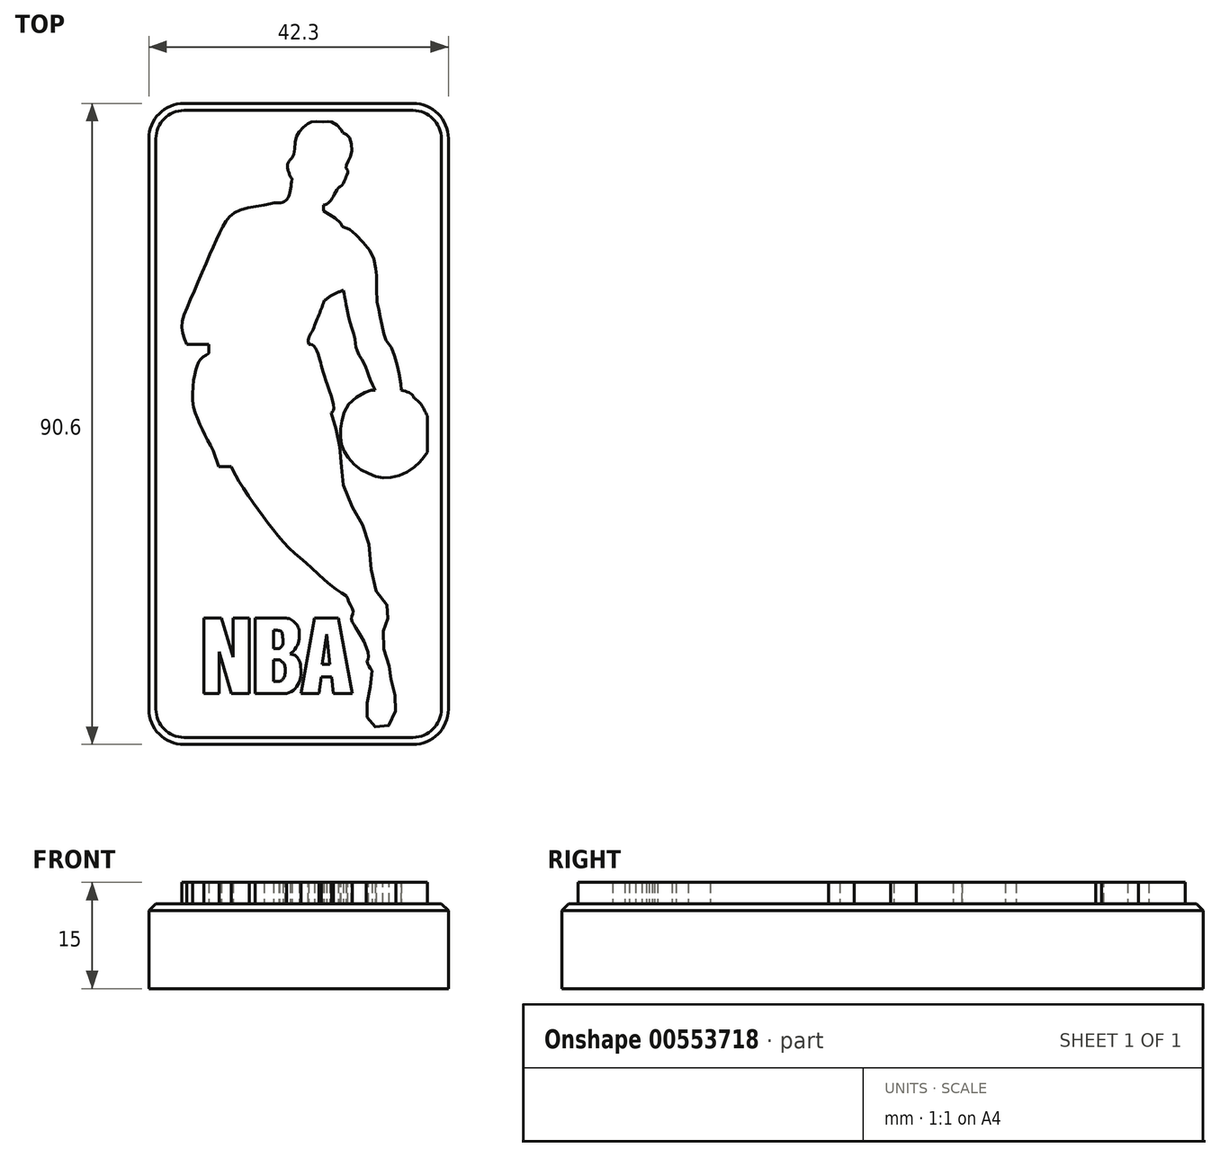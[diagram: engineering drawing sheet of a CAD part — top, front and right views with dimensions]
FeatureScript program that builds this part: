
annotation { "Feature Type Name" : "Feature", "Feature Type Description" : "" }
export const myFeature = defineFeature(function(context is Context, id is Id, definition is map)
    precondition{}
    {
        {
            var Q0;
            Q0=qCreatedBy(makeId("Top.planeOp"),FACE);
            var sketch = newSketch(context, id + "F0", { "sketchPlane" : qUnion([Q0])});
            skLineSegment(sketch, "E0", {"start": v(49.46, 96.34) * mm, "end": v(49.46, 0) * mm, "construction": true});
            skLineSegment(sketch, "E1", {"start": v(0, 48.17) * mm, "end": v(98.91, 48.17) * mm, "construction": true});
            skLineSegment(sketch, "E2.bottom", {"start": v(70.6, 93.47) * mm, "end": v(28.3, 93.47) * mm});
            skLineSegment(sketch, "E2.top", {"start": v(70.6, 2.87) * mm, "end": v(28.3, 2.87) * mm});
            skLineSegment(sketch, "E2.left", {"start": v(70.6, 93.47) * mm, "end": v(70.6, 2.87) * mm});
            skLineSegment(sketch, "E2.right", {"start": v(28.3, 93.47) * mm, "end": v(28.3, 2.87) * mm});
            skPoint(sketch, "E2.middle", {"position": v(49.46, 48.17) * mm});
            skSolve(sketch);
        }
        {
            var Q0;
            Q0=qSketchRegion(id+"F0",true);
            extrude(context, id + "F1", {"entities" : qUnion([Q0]), "depth" : 12 * mm, "offsetDistance" : 25 * mm});
        }
        {
            var Q0;
            Q0=qCreatedBy(makeId("Top.planeOp"),FACE);
            var sketch = newSketch(context, id + "F2", { "sketchPlane" : qUnion([Q0])});
            skLineSegment(sketch, "E3", {"start": v(36.08, 10.07) * mm, "end": v(36.06, 20.74) * mm});
            skLineSegment(sketch, "E4", {"start": v(36.06, 20.74) * mm, "end": v(38.53, 20.74) * mm});
            skLineSegment(sketch, "E5", {"start": v(38.53, 20.74) * mm, "end": v(40.2, 15.23) * mm});
            skLineSegment(sketch, "E6", {"start": v(40.2, 15.23) * mm, "end": v(40.2, 20.74) * mm});
            skLineSegment(sketch, "E7", {"start": v(40.2, 20.74) * mm, "end": v(42.53, 20.74) * mm});
            skLineSegment(sketch, "E8", {"start": v(42.53, 20.74) * mm, "end": v(42.53, 10.07) * mm});
            skLineSegment(sketch, "E9", {"start": v(42.53, 10.07) * mm, "end": v(39.96, 10.07) * mm});
            skLineSegment(sketch, "E10", {"start": v(39.96, 10.07) * mm, "end": v(38.25, 15.94) * mm});
            skLineSegment(sketch, "E11", {"start": v(38.25, 15.94) * mm, "end": v(38.25, 10.07) * mm});
            skLineSegment(sketch, "E12", {"start": v(38.25, 10.07) * mm, "end": v(36.08, 10.07) * mm});
            skLineSegment(sketch, "E13", {"start": v(43.32, 10.07) * mm, "end": v(43.3, 20.74) * mm});
            skLineSegment(sketch, "E14", {"start": v(43.3, 20.74) * mm, "end": v(47.68, 20.74) * mm});
            skLineSegment(sketch, "E15", {"start": v(43.32, 10.07) * mm, "end": v(47.75, 10.08) * mm});
            skFitSpline(sketch, "E16", {"points": [v(47.75, 10.08) * mm, v(48.77, 10.58) * mm, v(49.49, 11.58) * mm, v(49.77, 12.75) * mm, v(49.75, 13.92) * mm, v(49.51, 14.83) * mm, v(49.15, 15.29) * mm, v(48.83, 15.52) * mm, v(48.28, 15.65) * mm], "startDerivative": vector(7.59, 2.72) * mm, "endDerivative": vector(-5.94, 1) * mm});
            skFitSpline(sketch, "E17", {"points": [v(48.28, 15.65) * mm, v(48.94, 16.33) * mm, v(49.47, 17.44) * mm, v(49.53, 18.32) * mm, v(49.49, 19.2) * mm, v(49.21, 19.77) * mm, v(48.72, 20.3) * mm, v(48.28, 20.6) * mm, v(47.68, 20.74) * mm], "startDerivative": vector(4.95, 4.43) * mm, "endDerivative": vector(-5.76, 0.93) * mm});
            skLineSegment(sketch, "E18", {"start": v(45.94, 19) * mm, "end": v(45.94, 16.5) * mm});
            skFitSpline(sketch, "E19", {"points": [v(45.94, 19) * mm, v(46.53, 19) * mm, v(47, 18.82) * mm, v(47.2, 18.33) * mm, v(47.25, 17.67) * mm, v(47.25, 17.06) * mm, v(46.99, 16.64) * mm, v(46.7, 16.44) * mm], "startDerivative": vector(3.88, 0.21) * mm, "endDerivative": vector(-2.46, -1.47) * mm});
            skLineSegment(sketch, "E20", {"start": v(46.7, 16.44) * mm, "end": v(45.94, 16.44) * mm});
            skLineSegment(sketch, "E21", {"start": v(45.94, 16.44) * mm, "end": v(45.94, 16.5) * mm});
            skLineSegment(sketch, "E22", {"start": v(45.94, 14.83) * mm, "end": v(45.94, 11.81) * mm});
            skLineSegment(sketch, "E23", {"start": v(45.94, 11.81) * mm, "end": v(46.79, 11.81) * mm});
            skFitSpline(sketch, "E24", {"points": [v(46.79, 11.81) * mm, v(47.22, 12.07) * mm, v(47.53, 12.8) * mm, v(47.56, 13.65) * mm, v(47.4, 14.25) * mm, v(47, 14.66) * mm, v(46.79, 14.84) * mm], "startDerivative": vector(3, 1.25) * mm, "endDerivative": vector(-1.62, 1.47) * mm});
            skLineSegment(sketch, "E25", {"start": v(45.94, 14.83) * mm, "end": v(46.79, 14.84) * mm});
            skLineSegment(sketch, "E26", {"start": v(49.8, 10.08) * mm, "end": v(50.27, 10.08) * mm});
            skLineSegment(sketch, "E27", {"start": v(50.27, 10.08) * mm, "end": v(52.35, 10.09) * mm});
            skLineSegment(sketch, "E28", {"start": v(52.35, 10.09) * mm, "end": v(52.64, 12.4) * mm});
            skLineSegment(sketch, "E29", {"start": v(52.64, 12.4) * mm, "end": v(54.13, 12.4) * mm});
            skLineSegment(sketch, "E30", {"start": v(54.13, 12.4) * mm, "end": v(54.35, 10.08) * mm});
            skLineSegment(sketch, "E31", {"start": v(54.35, 10.08) * mm, "end": v(57.02, 10.1) * mm});
            skLineSegment(sketch, "E32", {"start": v(57.02, 10.1) * mm, "end": v(55.07, 20.7) * mm});
            skLineSegment(sketch, "E33", {"start": v(55.07, 20.7) * mm, "end": v(51.71, 20.7) * mm});
            skLineSegment(sketch, "E34", {"start": v(51.71, 20.7) * mm, "end": v(49.8, 10.08) * mm});
            skLineSegment(sketch, "E35", {"start": v(52.8, 14.19) * mm, "end": v(53.85, 14.19) * mm});
            skLineSegment(sketch, "E36", {"start": v(53.85, 14.19) * mm, "end": v(53.45, 18.42) * mm});
            skLineSegment(sketch, "E37", {"start": v(53.45, 18.42) * mm, "end": v(52.8, 14.19) * mm});
            skSolve(sketch);
        }
        {
            var Q0;
            Q0=qSketchRegion(id+"F2",true);
            extrude(context, id + "F3", {"entities" : qUnion([Q0]), "operationType" : NewBodyOperationType.ADD, "depth" : 15 * mm, "offsetDistance" : 25 * mm});
        }
        {
            var Q0;
            Q0=qCreatedBy(makeId("Top.planeOp"),FACE);
            var sketch = newSketch(context, id + "F4", { "sketchPlane" : qUnion([Q0])});
            skFitSpline(sketch, "E38", {"points": [v(56.13, 84.27) * mm, v(56.38, 84.06) * mm, v(56.32, 83.43) * mm, v(56.07, 82.86) * mm, v(55.63, 81.93) * mm, v(55.23, 81.64) * mm, v(55.06, 81.53) * mm, v(54.6, 80.79) * mm, v(54.22, 80.1) * mm, v(53.88, 79.58) * mm, v(53.44, 79.24) * mm, v(52.94, 79.1) * mm], "startDerivative": vector(4.5, -2.2) * mm, "endDerivative": vector(-5.95, -1.06) * mm});
            skFitSpline(sketch, "E39", {"points": [v(52.94, 79.1) * mm, v(52.94, 78.25) * mm], "startDerivative": vector(0, -0.86) * mm, "endDerivative": vector(0, -0.86) * mm});
            skFitSpline(sketch, "E40", {"points": [v(52.94, 78.25) * mm, v(55.23, 76.82) * mm, v(55.42, 76.5) * mm, v(55.44, 76.18) * mm, v(56.1, 75.95) * mm, v(57.05, 75.4) * mm, v(58.11, 74.32) * mm, v(59.44, 72.75) * mm, v(60.08, 71.4) * mm, v(60.4, 69.88) * mm, v(60.48, 68.98) * mm, v(60.5, 65.62) * mm, v(60.72, 64.46) * mm, v(60.95, 63.55) * mm, v(61.19, 62.38) * mm, v(61.46, 61.03) * mm, v(61.64, 60.25) * mm, v(62.44, 59.13) * mm, v(63.02, 57.81) * mm, v(63.42, 56.2) * mm, v(63.72, 55.04) * mm, v(63.95, 53.3) * mm, v(63.93, 52.94) * mm], "startDerivative": vector(43.04, -24.8) * mm, "endDerivative": vector(-1.36, -11.13) * mm});
            skFitSpline(sketch, "E41", {"points": [v(63.93, 52.94) * mm, v(65.3, 52.44) * mm, v(65.82, 51.82) * mm, v(66.57, 51.15) * mm, v(67.18, 50.18) * mm, v(67.65, 49.33) * mm], "startDerivative": vector(6.8, -1.68) * mm, "endDerivative": vector(2.4, -4.31) * mm});
            skFitSpline(sketch, "E42", {"points": [v(67.65, 49.33) * mm, v(67.65, 44.18) * mm], "startDerivative": vector(0, -5.16) * mm, "endDerivative": vector(0, -5.16) * mm});
            skFitSpline(sketch, "E43", {"points": [v(67.65, 44.18) * mm, v(66.97, 43.24) * mm, v(66.13, 42.32) * mm, v(64.47, 41.17) * mm, v(62.47, 40.6) * mm, v(60.8, 40.62) * mm, v(59.17, 41.23) * mm, v(57.4, 42.34) * mm, v(56.09, 43.95) * mm, v(55.52, 45.24) * mm, v(55.39, 47.05) * mm, v(55.66, 48.91) * mm, v(56.6, 51.04) * mm, v(58.92, 52.66) * mm, v(59.94, 52.94) * mm, v(60.26, 52.94) * mm], "startDerivative": vector(-11.97, -17.16) * mm, "endDerivative": vector(9.83, -0.58) * mm});
            skFitSpline(sketch, "E44", {"points": [v(60.26, 52.94) * mm, v(59.23, 55.35) * mm, v(58.66, 56.77) * mm, v(57.7, 58.56) * mm, v(57.43, 59.99) * mm, v(56.7, 62.7) * mm, v(56.23, 64.65) * mm, v(55.98, 66) * mm, v(55.78, 67.05) * mm], "startDerivative": vector(-7.83, 17.22) * mm, "endDerivative": vector(-2.09, 10.68) * mm});
            skFitSpline(sketch, "E45", {"points": [v(55.78, 67.05) * mm, v(54.3, 66.44) * mm, v(53.03, 65.52) * mm], "startDerivative": vector(-3.05, -1.05) * mm, "endDerivative": vector(-2.45, -2) * mm});
            skFitSpline(sketch, "E46", {"points": [v(53.03, 65.52) * mm, v(52.58, 64.2) * mm, v(51.95, 62.72) * mm, v(51.36, 61.21) * mm, v(50.82, 60.12) * mm, v(50.91, 59.4) * mm], "startDerivative": vector(-1.92, -6.3) * mm, "endDerivative": vector(1.44, -4.65) * mm});
            skFitSpline(sketch, "E47", {"points": [v(50.91, 59.4) * mm, v(51.55, 59.24) * mm, v(52.44, 57.38) * mm, v(53.03, 55.16) * mm, v(54.43, 50.33) * mm, v(54.05, 49.77) * mm], "startDerivative": vector(5.44, 0.14) * mm, "endDerivative": vector(-4.4, -2.9) * mm});
            skFitSpline(sketch, "E48", {"points": [v(54.05, 49.77) * mm, v(54.73, 47.48) * mm, v(55.23, 45.12) * mm, v(55.52, 41.97) * mm, v(55.78, 39.46) * mm, v(57.5, 35.56) * mm, v(58.9, 33.04) * mm, v(59.62, 29) * mm, v(60.26, 24.8) * mm, v(61.78, 22.84) * mm, v(62.25, 21.32) * mm, v(61.75, 19.99) * mm, v(61.41, 18.58) * mm, v(61.55, 15.9) * mm, v(62.25, 13.82) * mm, v(62.39, 12.62) * mm, v(62.93, 10.42) * mm, v(63.18, 8.86) * mm, v(62.96, 6.61) * mm, v(61.78, 5.28) * mm, v(60.26, 5.35) * mm, v(59.38, 6.27) * mm, v(59.04, 7.27) * mm, v(59.24, 9.2) * mm, v(59.62, 11.3) * mm, v(59.8, 13.32) * mm], "startDerivative": vector(17.19, -55.33) * mm, "endDerivative": vector(3.4, 52.46) * mm});
            skFitSpline(sketch, "E49", {"points": [v(59.8, 13.32) * mm, v(59.38, 13.98) * mm, v(59.13, 14.61) * mm, v(59.35, 15.3) * mm, v(58.15, 18.35) * mm, v(57.15, 19.96) * mm, v(56.93, 20.92) * mm, v(57.18, 21.57) * mm, v(56.68, 22.77) * mm, v(56.25, 23.86) * mm], "startDerivative": vector(-4.75, 7.09) * mm, "endDerivative": vector(-3.14, 9.49) * mm});
            skFitSpline(sketch, "E50", {"points": [v(56.25, 23.86) * mm, v(54.05, 25.32) * mm, v(50.91, 28.18) * mm, v(48.25, 30.48) * mm, v(45.53, 33.66) * mm, v(43.03, 37.06) * mm, v(40.69, 40.68) * mm, v(39.95, 42.15) * mm], "startDerivative": vector(-17, 10) * mm, "endDerivative": vector(-6.02, 13.27) * mm});
            skFitSpline(sketch, "E51", {"points": [v(39.95, 42.15) * mm, v(38.15, 42.15) * mm], "startDerivative": vector(-1.8, 0) * mm, "endDerivative": vector(-1.8, 0) * mm});
            skFitSpline(sketch, "E52", {"points": [v(38.15, 42.15) * mm, v(37.48, 44.18) * mm, v(36.33, 46.41) * mm, v(35.3, 48.66) * mm, v(34.52, 51.21) * mm, v(34.68, 54.49) * mm, v(35.06, 56.2) * mm, v(35.44, 57.08) * mm, v(36.09, 57.7) * mm, v(36.8, 58.11) * mm], "startDerivative": vector(-4.74, 16.89) * mm, "endDerivative": vector(9.78, 5.16) * mm});
            skFitSpline(sketch, "E53", {"points": [v(36.8, 58.11) * mm, v(36.8, 59.4) * mm], "startDerivative": vector(0, 1.3) * mm, "endDerivative": vector(0, 1.3) * mm});
            skFitSpline(sketch, "E54", {"points": [v(36.8, 59.4) * mm, v(33.68, 59.4) * mm], "startDerivative": vector(-3.13, 0) * mm, "endDerivative": vector(-3.13, 0) * mm});
            skFitSpline(sketch, "E55", {"points": [v(33.68, 59.4) * mm, v(32.96, 61.88) * mm, v(34.1, 65.52) * mm, v(36.8, 71.87) * mm, v(38.68, 75.91) * mm, v(40.4, 78) * mm, v(44.62, 79.07) * mm], "startDerivative": vector(-8.1, 18.08) * mm, "endDerivative": vector(27.69, 3.84) * mm});
            skFitSpline(sketch, "E56", {"points": [v(44.62, 79.07) * mm, v(45.92, 79.38) * mm, v(46.95, 79.42) * mm, v(47.86, 79.95) * mm, v(48.24, 80.94) * mm, v(48.51, 82.77) * mm], "startDerivative": vector(6.45, 2) * mm, "endDerivative": vector(1.03, 8.03) * mm});
            skFitSpline(sketch, "E57", {"points": [v(48.51, 82.77) * mm, v(48.02, 83.84) * mm, v(47.94, 84.94) * mm, v(48.51, 85.74) * mm], "startDerivative": vector(-1.61, 2.97) * mm, "endDerivative": vector(2.25, 2.32) * mm});
            skFitSpline(sketch, "E58", {"points": [v(48.51, 85.74) * mm, v(48.85, 86.5) * mm, v(49.05, 88.41) * mm, v(49.7, 89.67) * mm, v(50.91, 90.7) * mm, v(51.52, 90.9) * mm, v(53.31, 90.85) * mm, v(54.05, 90.9) * mm, v(55.33, 89.86) * mm, v(55.78, 89.25) * mm, v(56.36, 88.98) * mm, v(56.97, 87.38) * mm, v(56.7, 85.74) * mm, v(56.23, 84.8) * mm, v(56.13, 84.27) * mm], "startDerivative": vector(6.68, 10.5) * mm, "endDerivative": vector(-0.94, -10.26) * mm});
            skSolve(sketch);
        }
        {
            var Q0;
            Q0=qSketchRegion(id+"F4",true);
            extrude(context, id + "F5", {"entities" : qUnion([Q0]), "operationType" : NewBodyOperationType.ADD, "depth" : 15 * mm, "offsetDistance" : 25 * mm});
        }
        {
            var Q0;
            Q0=makeQuery(id+"F1.opExtrude","SWEPT_EDGE",EDGE,{"disambiguationData":[OSD([sQuery(id+"F0.wireOp",EDGE,"E2.bottom"),sQuery(id+"F0.wireOp",EDGE,"E2.right")])]});
            var Q1;
            Q1=makeQuery(id+"F1.opExtrude","SWEPT_EDGE",EDGE,{"disambiguationData":[OSD([sQuery(id+"F0.wireOp",EDGE,"E2.bottom"),sQuery(id+"F0.wireOp",EDGE,"E2.left")])]});
            var Q2;
            Q2=makeQuery(id+"F1.opExtrude","SWEPT_EDGE",EDGE,{"disambiguationData":[OSD([sQuery(id+"F0.wireOp",EDGE,"E2.top"),sQuery(id+"F0.wireOp",EDGE,"E2.right")])]});
            var Q3;
            Q3=makeQuery(id+"F1.opExtrude","SWEPT_EDGE",EDGE,{"disambiguationData":[OSD([sQuery(id+"F0.wireOp",EDGE,"E2.top"),sQuery(id+"F0.wireOp",EDGE,"E2.left")])]});
            fillet(context, id + "F6", {"entities" : qUnion([Q0, Q1, Q2, Q3]), "radius" : 5 * mm, "tangentPropagation" : true, "allowEdgeOverflow" : false});
        }
        {
            var Q0;
            Q0=makeQuery(id+"F1.opExtrude","CAP_EDGE",EDGE,{"disambiguationData":[OSD([sQuery(id+"F0.wireOp",EDGE,"E2.right")])],"isStart":false});
            chamfer(context, id + "F7", {"entities" : qUnion([Q0]), "width" : 1 * mm, "tangentPropagation" : true});
        }
    });
